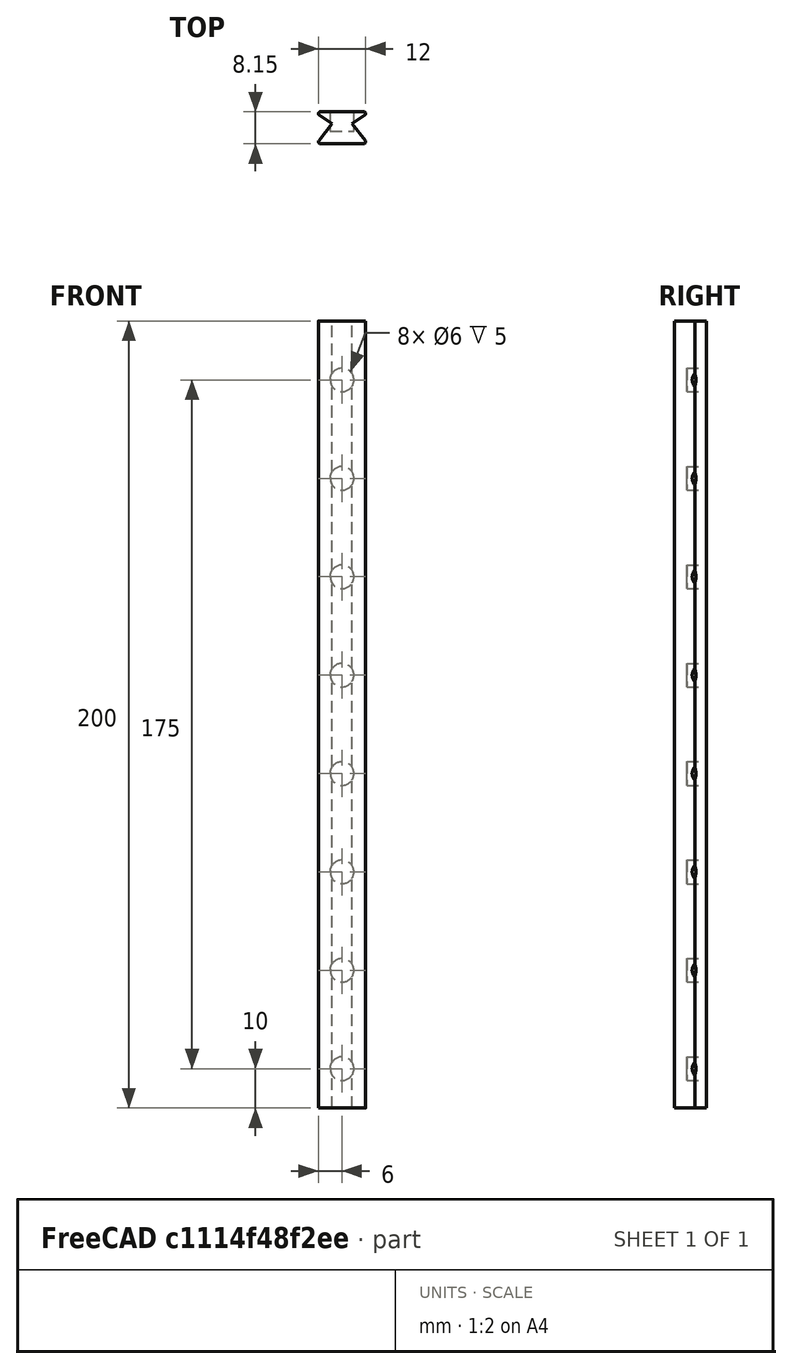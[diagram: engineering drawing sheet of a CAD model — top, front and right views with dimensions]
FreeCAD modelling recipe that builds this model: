
FCSTD DOCUMENT  (FreeCAD 0.21R33771 (Git))
Label: Guida-quadra-12
License: All rights reserved
LicenseURL: https://en.wikipedia.org/wiki/All_rights_reserved
objects: Sketcher::SketchObject×3, PartDesign::CoordinateSystem×1, PartDesign::Pocket×1, PartDesign::Body×1
note: 7 computed .brp shape members not serialized (recipe doc carries the construction recipe); baked Part::Feature solids carry a one-line shape summary decoded from their .brp

FEATURE [Sketcher::SketchObject] Sketch
  FullyConstrained = true
  MapMode = 5
  Support = -> [XY_Plane]
  sketch-geometry (10):
    g0: LineSegment StartX=-5.5 StartY=0 StartZ=0 EndX=5.5 EndY=0 EndZ=0
    g1: LineSegment StartX=5.5 StartY=8.15196 StartZ=0 EndX=-5.5 EndY=8.15196 EndZ=0
    g2: LineSegment StartX=-5.76828 StartY=7.23003 StartZ=0 EndX=-2.5 EndY=5.15196 EndZ=0
    g3: LineSegment StartX=-2.5 StartY=5.15196 StartZ=0 EndX=-5.89401 EndY=0.807831 EndZ=0
    g4: LineSegment StartX=5.76828 StartY=7.23003 StartZ=0 EndX=2.5 EndY=5.15196 EndZ=0
    g5: LineSegment StartX=2.5 StartY=5.15196 StartZ=0 EndX=5.89401 EndY=0.807831 EndZ=0
    g6: ArcOfCircle CenterX=-5.5 CenterY=0.5 CenterZ=0 NormalX=0 NormalY=0 NormalZ=1 AngleXU=0 Radius=0.5 StartAngle=2.47837 EndAngle=4.71239
    g7: ArcOfCircle CenterX=5.5 CenterY=0.5 CenterZ=0 NormalX=0 NormalY=0 NormalZ=1 AngleXU=0 Radius=0.5 StartAngle=4.71239 EndAngle=6.94641
    g8: ArcOfCircle CenterX=-5.5 CenterY=7.65196 CenterZ=0 NormalX=0 NormalY=0 NormalZ=1 AngleXU=0 Radius=0.5 StartAngle=1.5708 EndAngle=4.14604
    g9: ArcOfCircle CenterX=5.5 CenterY=7.65196 CenterZ=0 NormalX=0 NormalY=0 NormalZ=1 AngleXU=0 Radius=0.5 StartAngle=5.27874 EndAngle=7.85398
  constraints (23):
    c: Coincident(g3,g2)
    c: Coincident(g5,g4)
    c: Equal(g0,g1)
    c: Tangent(g3,g6) = -1.5708
    c: Tangent(g0,g6) = -1.5708
    c: Tangent(g5,g7) = 1.5708
    c: Tangent(g0,g7) = -1.5708
    c: Radius(g7) = 0.5
    c: Equal(g6,g7)
    c: Tangent(g2,g8) = -1.5708
    c: Tangent(g1,g8) = -1.5708
    c: Tangent(g1,g9) = -1.5708
    c: Tangent(g4,g9) = 1.5708
    c: Symmetric(g6,g7,g-2)
    c: Symmetric(g8,g9,g-2)
    c: Equal(g7,g9)
    c: Equal(g9,g8)
    c: Symmetric(g2,g4,g-2)
    c: DistanceX(g6,g7) = 11
    c: DistanceY(g4,g9) = 2.5
    c: DistanceX(g2,g-1) = 2.5
    c: PointOnObject(g-1,g0)
    c: Angle(g5,g0) = 0.907571
FEATURE [Sketcher::SketchObject] Sketch001
  FullyConstrained = true
  MapMode = 5
  Placement = pos=(0,8.15196,0) rot=(0,0.707107,0.707107;3.14159rad)
  sketch-geometry (15):
    g0: Circle CenterX=0 CenterY=10 CenterZ=0 NormalX=0 NormalY=0 NormalZ=1 AngleXU=0 Radius=1.5
    g1: Circle CenterX=0 CenterY=35 CenterZ=0 NormalX=0 NormalY=0 NormalZ=1 AngleXU=0 Radius=1.5
    g2: LineSegment StartX=0 StartY=10 StartZ=0 EndX=0 EndY=35 EndZ=0
    g3: Circle CenterX=-1.6081e-12 CenterY=60 CenterZ=0 NormalX=0 NormalY=0 NormalZ=1 AngleXU=0 Radius=1.5
    g4: LineSegment StartX=0 StartY=35 StartZ=0 EndX=-1.6081e-12 EndY=60 EndZ=0
    g5: Circle CenterX=-2.2222e-12 CenterY=85 CenterZ=0 NormalX=0 NormalY=0 NormalZ=1 AngleXU=0 Radius=1.5
    g6: LineSegment StartX=-1.6081e-12 StartY=60 StartZ=0 EndX=-2.2222e-12 EndY=85 EndZ=0
    g7: Circle CenterX=-3.5638e-12 CenterY=110 CenterZ=0 NormalX=0 NormalY=0 NormalZ=1 AngleXU=0 Radius=1.5
    g8: LineSegment StartX=-2.2222e-12 StartY=85 StartZ=0 EndX=-3.5638e-12 EndY=110 EndZ=0
    g9: Circle CenterX=-4.2007e-12 CenterY=135 CenterZ=0 NormalX=0 NormalY=0 NormalZ=1 AngleXU=0 Radius=1.5
    g10: LineSegment StartX=-3.5638e-12 StartY=110 StartZ=0 EndX=-4.2007e-12 EndY=135 EndZ=0
    g11: Circle CenterX=-5.3491e-12 CenterY=160 CenterZ=0 NormalX=0 NormalY=0 NormalZ=1 AngleXU=0 Radius=1.5
    g12: LineSegment StartX=-4.2007e-12 StartY=135 StartZ=0 EndX=-5.3491e-12 EndY=160 EndZ=0
    g13: Circle CenterX=-6.3104e-12 CenterY=185 CenterZ=0 NormalX=0 NormalY=0 NormalZ=1 AngleXU=0 Radius=1.5
    g14: LineSegment StartX=-5.3491e-12 StartY=160 StartZ=0 EndX=-6.3104e-12 EndY=185 EndZ=0
  constraints (38):
    c: PointOnObject(g0,g-2)
    c: Radius(g0) = 1.5
    c: DistanceY(g-1,g0) = 10
    c: Radius(g1) = 1.5
    c: Coincident(g0,g2)
    c: Coincident(g1,g2)
    c: Distance(g2) = 25
    c: Radius(g3) = 1.5
    c: Coincident(g1,g4)
    c: Coincident(g3,g4)
    c: Equal(g2,g4)
    c: Parallel(g4,g2)
    c: Radius(g5) = 1.5
    c: Coincident(g3,g6)
    c: Coincident(g5,g6)
    c: Equal(g2,g6)
    c: Parallel(g6,g2)
    c: Radius(g7) = 1.5
    c: Coincident(g5,g8)
    c: Coincident(g7,g8)
    c: Equal(g2,g8)
    c: Parallel(g8,g2)
    c: Radius(g9) = 1.5
    c: Coincident(g7,g10)
    c: Coincident(g9,g10)
    c: Equal(g2,g10)
    c: Parallel(g10,g2)
    c: Radius(g11) = 1.5
    c: Coincident(g9,g12)
    c: Coincident(g11,g12)
    c: Equal(g2,g12)
    c: Parallel(g12,g2)
    c: Radius(g13) = 1.5
    c: Coincident(g11,g14)
    c: Coincident(g13,g14)
    c: Equal(g2,g14)
    c: Parallel(g14,g2)
    c: PointOnObject(g1,g-2)
FEATURE [PartDesign::CoordinateSystem] LCS_GuidaQuadra12
  AttacherType = Attacher::AttachEngine3D
FEATURE [Sketcher::SketchObject] Sketch002
  FullyConstrained = false
  MapMode = 5
  Placement = pos=(0,8.15196,0) rot=(0,0.707107,0.707107;3.14159rad)
  sketch-geometry (8):
    g0: Circle CenterX=0 CenterY=185 CenterZ=0 NormalX=0 NormalY=0 NormalZ=1 AngleXU=0 Radius=3
    g1: Circle CenterX=0 CenterY=160 CenterZ=0 NormalX=0 NormalY=0 NormalZ=1 AngleXU=0 Radius=3
    g2: Circle CenterX=0 CenterY=135 CenterZ=0 NormalX=0 NormalY=0 NormalZ=1 AngleXU=0 Radius=3
    g3: Circle CenterX=0 CenterY=110 CenterZ=0 NormalX=0 NormalY=0 NormalZ=1 AngleXU=0 Radius=3
    g4: Circle CenterX=0 CenterY=85 CenterZ=0 NormalX=0 NormalY=0 NormalZ=1 AngleXU=0 Radius=3
    g5: Circle CenterX=0 CenterY=60 CenterZ=0 NormalX=0 NormalY=0 NormalZ=1 AngleXU=0 Radius=3
    g6: Circle CenterX=0 CenterY=35 CenterZ=0 NormalX=0 NormalY=0 NormalZ=1 AngleXU=0 Radius=3
    g7: Circle CenterX=0 CenterY=10 CenterZ=0 NormalX=0 NormalY=0 NormalZ=1 AngleXU=0 Radius=3
  constraints (8):
    c: Radius(g0) = 3
    c: Equal(g0,g1)
    c: Equal(g1,g2)
    c: Equal(g2,g3)
    c: Equal(g3,g4)
    c: Equal(g4,g5)
    c: Equal(g5,g6)
    c: Equal(g6,g7)
FEATURE [PartDesign::Pocket] Pocket001
  Direction = (0,-1,2e-16)
  Length = 5
  Length2 = 5
  Profile = -> Sketch002
  ReferenceAxis = -> Sketch002 [N_Axis]
  Type = 0
FEATURE [PartDesign::Body] Body
  Group = -> [Sketch,Sketch001,LCS_GuidaQuadra12,Sketch002,Pocket001]
  Origin = -> Origin
  Tip = -> Pocket001
